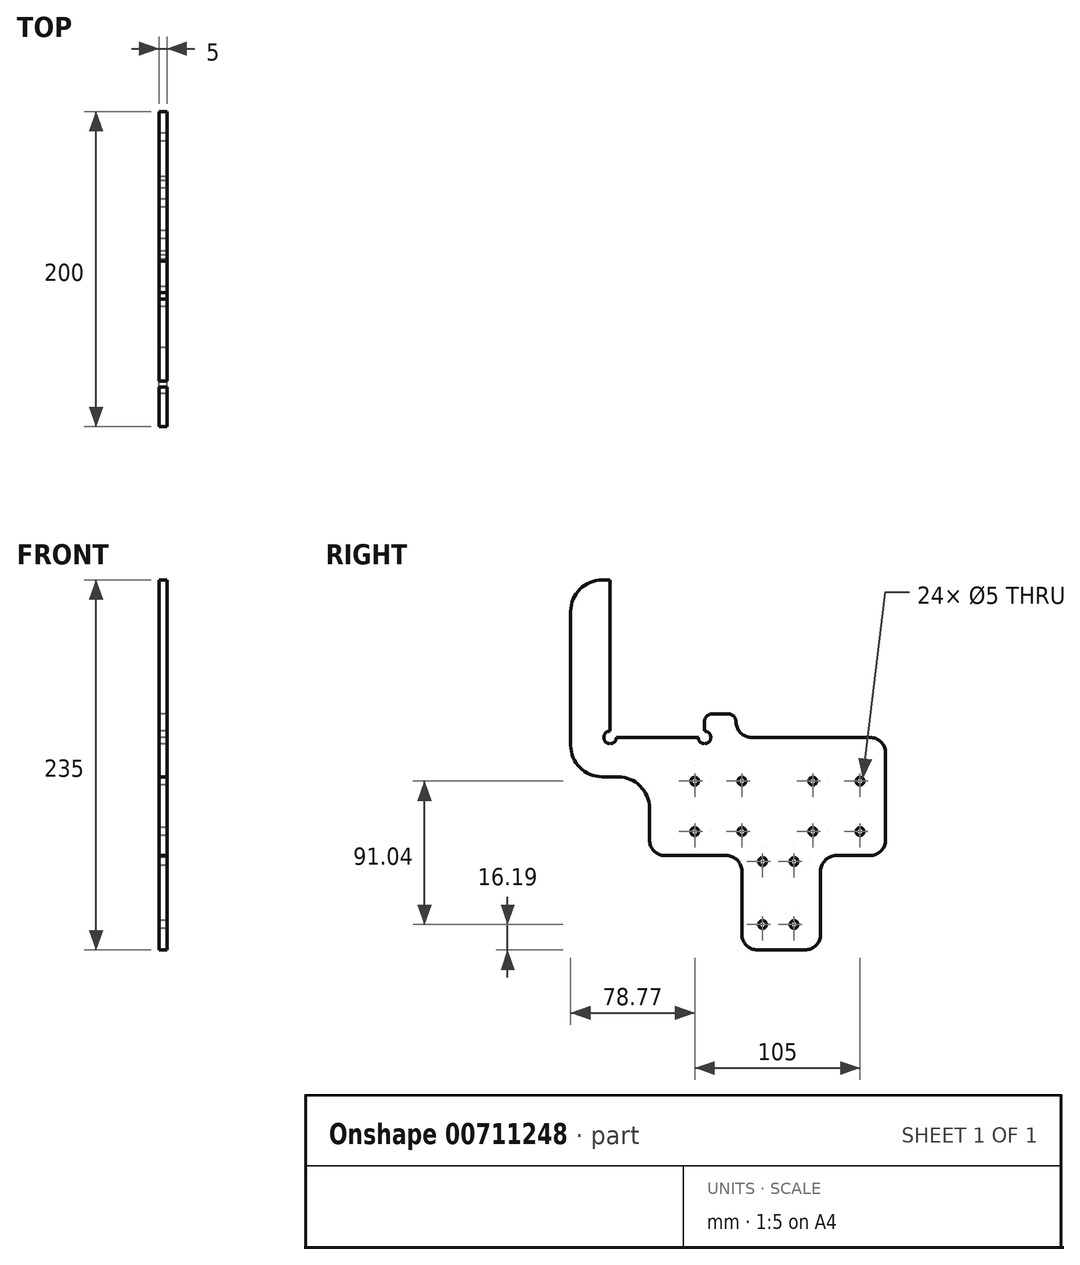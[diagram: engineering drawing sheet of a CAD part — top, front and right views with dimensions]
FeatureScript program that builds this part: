
annotation { "Feature Type Name" : "Feature", "Feature Type Description" : "" }
export const myFeature = defineFeature(function(context is Context, id is Id, definition is map)
    precondition{}
    {
        {
            var Q0;
            Q0=qCreatedBy(makeId("Right.planeOp"),FACE);
            var sketch = newSketch(context, id + "F0", { "sketchPlane" : qUnion([Q0])});
            skLineSegment(sketch, "E0.top", {"start": v(65, -37.5) * mm, "end": v(43.73, -37.5) * mm});
            skLineSegment(sketch, "E0.left", {"start": v(75, 27.5) * mm, "end": v(75, -27.5) * mm});
            skLineSegment(sketch, "E0.right", {"start": v(-75, -7.5) * mm, "end": v(-75, -27.5) * mm});
            skPoint(sketch, "E0.middle", {"position": v(0, 0) * mm});
            skLineSegment(sketch, "E1", {"start": v(-95, 12.5) * mm, "end": v(-105, 12.5) * mm});
            skLineSegment(sketch, "E2.0", {"start": v(-100, 137.5) * mm, "end": v(-105, 137.5) * mm});
            skLineSegment(sketch, "E3", {"start": v(-125, 32.5) * mm, "end": v(-125, 117.5) * mm});
            skLineSegment(sketch, "E4.0", {"start": v(-100, 41.5) * mm, "end": v(-100, 137.5) * mm});
            skLineSegment(sketch, "E5", {"start": v(65, 37.5) * mm, "end": v(-10, 37.5) * mm});
            skLineSegment(sketch, "E6.0", {"start": v(-40, 41.5) * mm, "end": v(-40, 47.5) * mm});
            skLineSegment(sketch, "E7.0", {"start": v(-20, 47.5) * mm, "end": v(-20, 47.5) * mm});
            skLineSegment(sketch, "E8.0", {"start": v(-25, 52.5) * mm, "end": v(-35, 52.5) * mm});
            skLineSegment(sketch, "E9.trimOffspring", {"start": v(-44, 37.5) * mm, "end": v(-96, 37.5) * mm});
            skPoint(sketch, "E10.visualSharp", {"position": v(-125, 137.5) * mm});
            skArc(sketch, "E10.filletArc", {"start": v(-105, 137.5) * mm, "mid": v(-119.14, 131.64) * mm, "end": v(-125, 117.5) * mm});
            skPoint(sketch, "E11.visualSharp", {"position": v(-125, 12.5) * mm});
            skArc(sketch, "E11.filletArc", {"start": v(-125, 32.5) * mm, "mid": v(-119.14, 18.36) * mm, "end": v(-105, 12.5) * mm});
            skPoint(sketch, "E12.visualSharp", {"position": v(-75, 12.5) * mm});
            skArc(sketch, "E12.filletArc", {"start": v(-75, -7.5) * mm, "mid": v(-80.86, 6.64) * mm, "end": v(-95, 12.5) * mm});
            skPoint(sketch, "E13.visualSharp", {"position": v(-75, -37.5) * mm});
            skArc(sketch, "E13.filletArc", {"start": v(-75, -27.5) * mm, "mid": v(-72.07, -34.57) * mm, "end": v(-65, -37.5) * mm});
            skLineSegment(sketch, "E14", {"start": v(-16.27, -47.5) * mm, "end": v(-16.27, -87.5) * mm});
            skLineSegment(sketch, "E15.0", {"start": v(33.73, -47.5) * mm, "end": v(33.73, -87.5) * mm});
            skLineSegment(sketch, "E16.0", {"start": v(23.73, -97.5) * mm, "end": v(-6.27, -97.5) * mm});
            skLineSegment(sketch, "E17.trimOffspring", {"start": v(-26.27, -37.5) * mm, "end": v(-65, -37.5) * mm});
            skPoint(sketch, "E18.visualSharp", {"position": v(-16.27, -37.5) * mm});
            skArc(sketch, "E18.filletArc", {"start": v(-16.27, -47.5) * mm, "mid": v(-19.2, -40.43) * mm, "end": v(-26.27, -37.5) * mm});
            skPoint(sketch, "E19.visualSharp", {"position": v(33.73, -37.5) * mm});
            skArc(sketch, "E19.filletArc", {"start": v(43.73, -37.5) * mm, "mid": v(36.66, -40.43) * mm, "end": v(33.73, -47.5) * mm});
            skPoint(sketch, "E20.visualSharp", {"position": v(-16.27, -97.5) * mm});
            skArc(sketch, "E20.filletArc", {"start": v(-16.27, -87.5) * mm, "mid": v(-13.34, -94.57) * mm, "end": v(-6.27, -97.5) * mm});
            skPoint(sketch, "E21.visualSharp", {"position": v(33.73, -97.5) * mm});
            skArc(sketch, "E21.filletArc", {"start": v(23.73, -97.5) * mm, "mid": v(30.8, -94.57) * mm, "end": v(33.73, -87.5) * mm});
            skPoint(sketch, "E22.visualSharp", {"position": v(75, -37.5) * mm});
            skArc(sketch, "E22.filletArc", {"start": v(65, -37.5) * mm, "mid": v(72.07, -34.57) * mm, "end": v(75, -27.5) * mm});
            skPoint(sketch, "E23.visualSharp", {"position": v(75, 37.5) * mm});
            skArc(sketch, "E23.filletArc", {"start": v(75, 27.5) * mm, "mid": v(72.07, 34.57) * mm, "end": v(65, 37.5) * mm});
            skPoint(sketch, "E24.visualSharp", {"position": v(-20, 37.5) * mm});
            skArc(sketch, "E24.filletArc", {"start": v(-20, 47.5) * mm, "mid": v(-17.07, 40.43) * mm, "end": v(-10, 37.5) * mm});
            skArc(sketch, "E25", {"start": v(-100, 41.5) * mm, "mid": v(-102.83, 34.67) * mm, "end": v(-96, 37.5) * mm});
            skArc(sketch, "E26", {"start": v(-44, 37.5) * mm, "mid": v(-37.17, 34.67) * mm, "end": v(-40, 41.5) * mm});
            skCircle(sketch, "E27", {"center": v(58.77, -22.27) * mm, "radius": 2.5 * mm});
            skCircle(sketch, "E28", {"center": v(58.77, 9.73) * mm, "radius": 2.5 * mm});
            skCircle(sketch, "E29", {"center": v(28.77, 9.73) * mm, "radius": 2.5 * mm});
            skCircle(sketch, "E30", {"center": v(28.77, -22.27) * mm, "radius": 2.5 * mm});
            skCircle(sketch, "E31", {"center": v(-16.23, -22.27) * mm, "radius": 2.5 * mm});
            skCircle(sketch, "E32", {"center": v(-16.23, 9.73) * mm, "radius": 2.5 * mm});
            skCircle(sketch, "E33", {"center": v(-46.23, 9.73) * mm, "radius": 2.5 * mm});
            skCircle(sketch, "E34", {"center": v(-46.23, -22.27) * mm, "radius": 2.5 * mm});
            skCircle(sketch, "E35", {"center": v(16.85, -81.3) * mm, "radius": 2.5 * mm});
            skCircle(sketch, "E36", {"center": v(16.85, -41.3) * mm, "radius": 2.5 * mm});
            skCircle(sketch, "E37", {"center": v(-3.15, -41.3) * mm, "radius": 2.5 * mm});
            skCircle(sketch, "E38", {"center": v(-3.15, -81.3) * mm, "radius": 2.5 * mm});
            skPoint(sketch, "E39.visualSharp", {"position": v(-40, 52.5) * mm});
            skArc(sketch, "E39.filletArc", {"start": v(-35, 52.5) * mm, "mid": v(-38.54, 51.04) * mm, "end": v(-40, 47.5) * mm});
            skPoint(sketch, "E40.visualSharp", {"position": v(-20, 52.5) * mm});
            skArc(sketch, "E40.filletArc", {"start": v(-20, 47.5) * mm, "mid": v(-21.46, 51.04) * mm, "end": v(-25, 52.5) * mm});
            skSolve(sketch);
        }
        {
            var Q0;
            Q0 = qSketchRegion(id + "F0", true);
            extrude(context, id + "F1", {"entities" : qUnion([Q0]), "depth" : 5 * mm, "offsetDistance" : 25 * mm});
        }
    });
